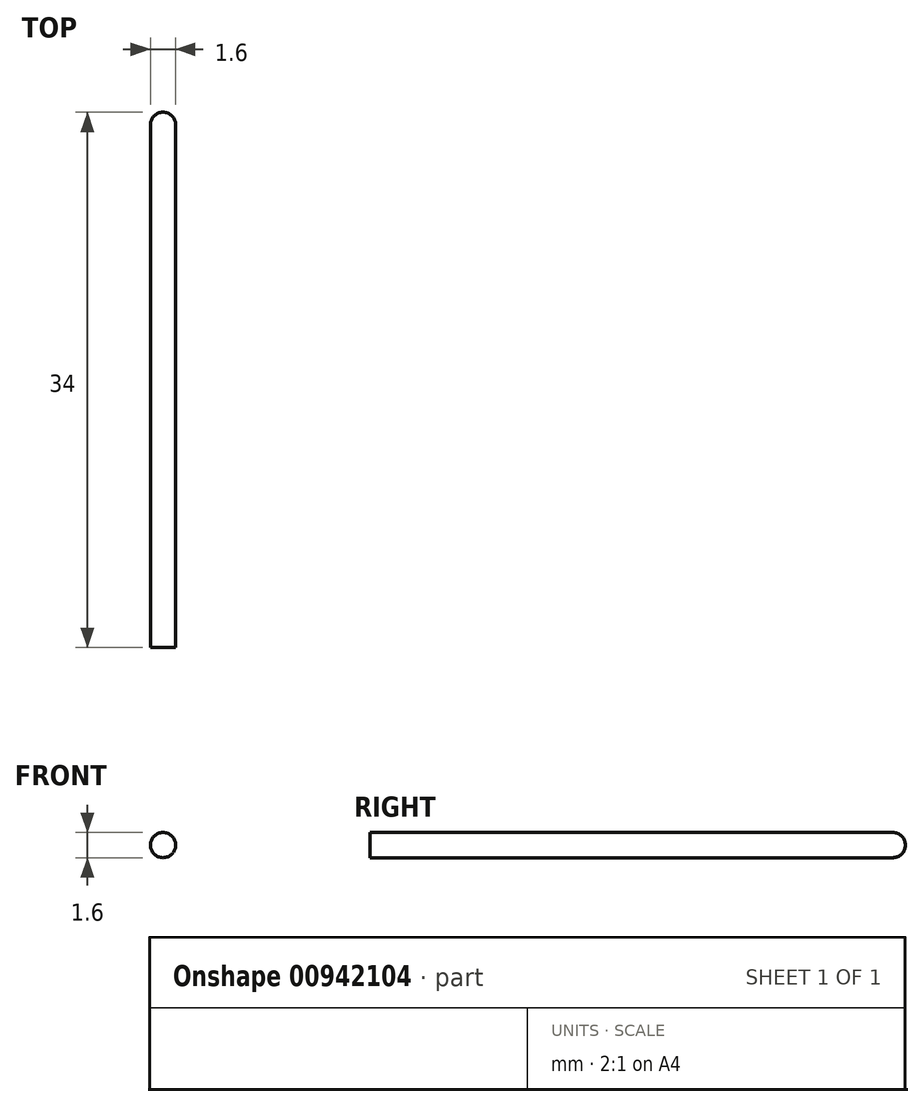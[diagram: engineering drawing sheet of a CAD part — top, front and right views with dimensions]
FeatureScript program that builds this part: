
annotation { "Feature Type Name" : "Feature", "Feature Type Description" : "" }
export const myFeature = defineFeature(function(context is Context, id is Id, definition is map)
    precondition{}
    {
        {
            var Q0;
            Q0=qCreatedBy(makeId("Front.planeOp"),FACE);
            var sketch = newSketch(context, id + "F0", { "sketchPlane" : qUnion([Q0])});
            skCircle(sketch, "E0", {"center": v(0, 0) * mm, "radius": 0.8 * mm});
            skSolve(sketch);
        }
        {
            var Q0;
            Q0 = qSketchRegion(id + "F0", true);
            extrude(context, id + "F1", {"entities" : qUnion([Q0]), "oppositeDirection" : true, "depth" : 34 * mm, "offsetDistance" : 25 * mm});
        }
        {
            var Q0;
            Q0=makeQuery(id+"F1.opExtrude","CAP_EDGE",EDGE,{"disambiguationData":[OSD([sQuery(id+"F0.wireOp",EDGE,"E0")])],"isStart":false});
            fillet(context, id + "F2", {"entities" : qUnion([Q0]), "radius" : 0.8 * mm, "tangentPropagation" : true, "allowEdgeOverflow" : false});
        }
    });
